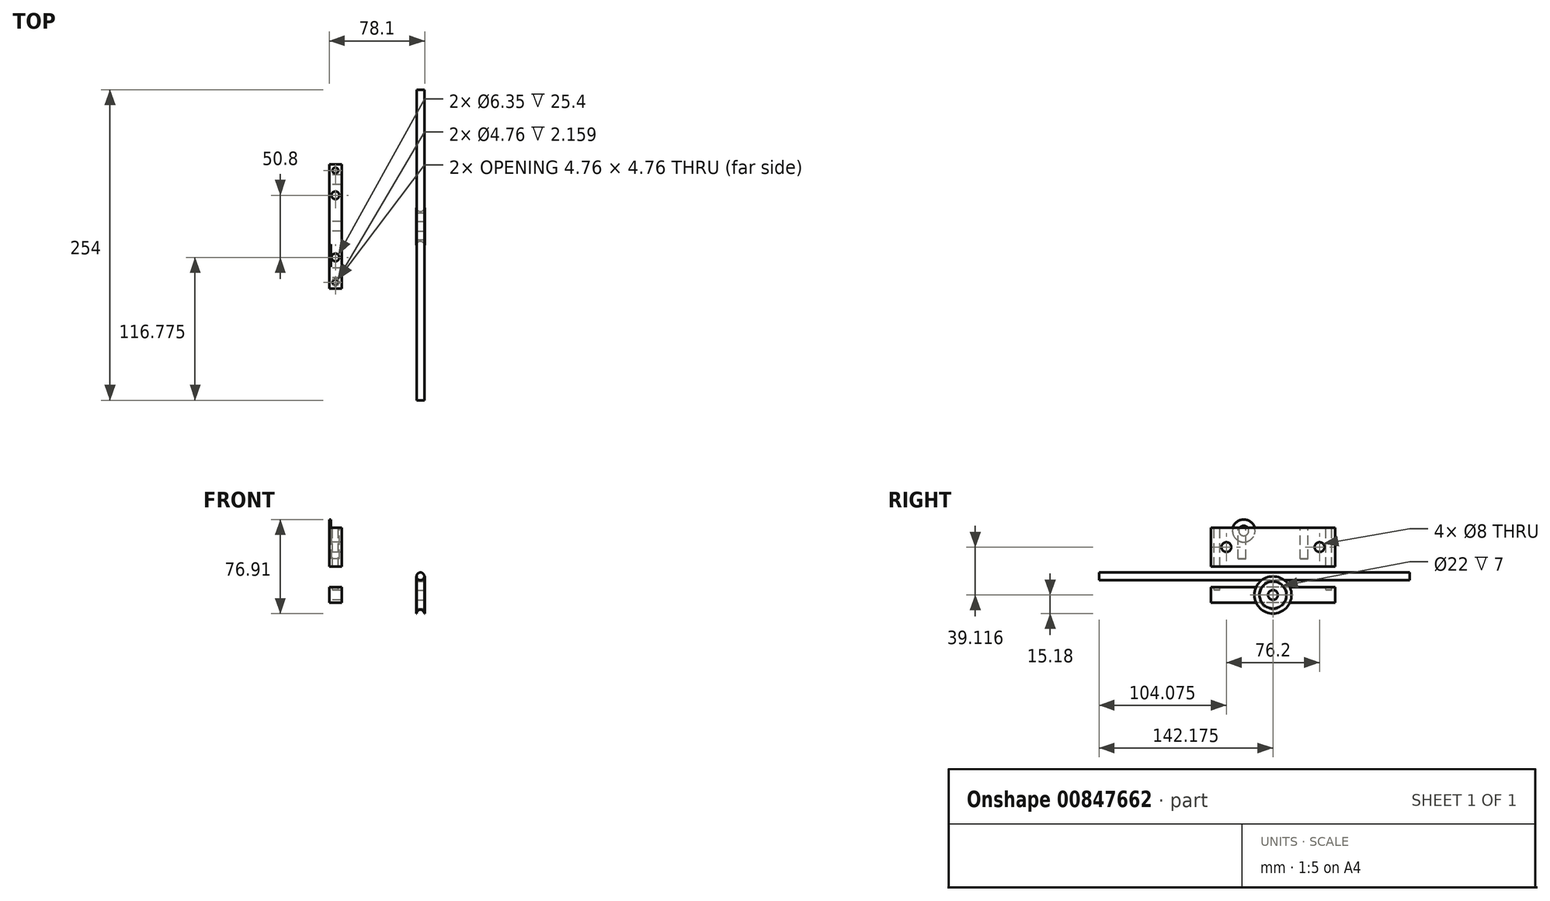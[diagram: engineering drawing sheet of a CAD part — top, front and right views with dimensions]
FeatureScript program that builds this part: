
annotation { "Feature Type Name" : "Feature", "Feature Type Description" : "" }
export const myFeature = defineFeature(function(context is Context, id is Id, definition is map)
    precondition{}
    {
        {
            var Q0;
            Q0=qCreatedBy(makeId("Top.planeOp"),FACE);
            var sketch = newSketch(context, id + "F0", { "sketchPlane" : qUnion([Q0])});
            skArc(sketch, "E0", {"start": v(77.77, 0) * mm, "mid": v(74.6, 3.18) * mm, "end": v(71.42, 0) * mm});
            skLineSegment(sketch, "E1", {"start": v(71.42, 0) * mm, "end": v(71.1, 0) * mm});
            skLineSegment(sketch, "E2", {"start": v(71.1, 0) * mm, "end": v(71.1, 3.18) * mm});
            skLineSegment(sketch, "E3", {"start": v(78.1, 3.18) * mm, "end": v(78.1, 0) * mm});
            skLineSegment(sketch, "E4", {"start": v(77.77, 0) * mm, "end": v(78.1, 0) * mm});
            skPoint(sketch, "E5.0", {"position": v(71.1, 15.18) * mm});
            skLineSegment(sketch, "E6", {"start": v(78.1, 15.18) * mm, "end": v(71.1, 15.18) * mm});
            skLineSegment(sketch, "E7", {"start": v(71.1, 4.18) * mm, "end": v(74.6, 4.18) * mm});
            skLineSegment(sketch, "E8", {"start": v(74.6, 4.18) * mm, "end": v(78.1, 4.18) * mm});
            skLineSegment(sketch, "E9", {"start": v(71.1, 15.18) * mm, "end": v(71.1, 4.18) * mm});
            skLineSegment(sketch, "E10", {"start": v(71.1, 4.18) * mm, "end": v(71.1, 3.18) * mm});
            skLineSegment(sketch, "E11", {"start": v(78.1, 15.18) * mm, "end": v(78.1, 4.18) * mm});
            skLineSegment(sketch, "E12", {"start": v(78.1, 4.18) * mm, "end": v(78.1, 3.18) * mm});
            skSolve(sketch);
        }
        {
            var Q0;
            Q0=qSketchRegion(id+"F0",true);
            var Q1;
            Q1=sQuery(id+"F0.wireOp",EDGE,"E6");
            revolve(context, id + "F1", {"surfaceOperationType" : NewSurfaceOperationType.NEW, "entities" : qUnion([Q0]), "axis" : qUnion([Q1]), "revolveType" : RevolveType.FULL, "oppositeDirection" : true});
        }
        {
            var Q0;
            Q0=makeQuery(id+"F0.imprint","IMPRINT",FACE,{"disambiguationData":[TD([[makeQuery(id+"F0.imprint","IMPRINT",EDGE,{"derivedFrom":sQuery(id+"F0.wireOp",EDGE,"E6")}),1.0]])]});
            var Q1;
            Q1=sQuery(id+"F0.wireOp",EDGE,"E6");
            revolve(context, id + "F2", {"operationType" : NewBodyOperationType.REMOVE, "surfaceOperationType" : NewSurfaceOperationType.NEW, "entities" : qUnion([Q0]), "axis" : qUnion([Q1]), "revolveType" : RevolveType.FULL, "oppositeDirection" : true});
        }
        {
            var Q0;
            Q0=makeQuery(id+"F1.opRevolve","SWEPT_FACE",FACE,{"disambiguationData":[OSD([sQuery(id+"F0.wireOp",EDGE,"E3"),sQuery(id+"F0.wireOp",EDGE,"E11"),sQuery(id+"F0.wireOp",EDGE,"E12")])]});
            var sketch = newSketch(context, id + "F3", { "sketchPlane" : qUnion([Q0])});
            skCircle(sketch, "E13", {"center": v(15.18, 0) * mm, "radius": 11 * mm});
            skCircle(sketch, "E14", {"center": v(15.18, 0) * mm, "radius": 4 * mm});
            skSolve(sketch);
        }
        {
            var Q0;
            Q0=qSketchRegion(id+"F3",true);
            var Q1;
            Q1=sQuery(id+"F3.wireOp",EDGE,"kzQAHwlb-sFjF-DyDI-pdxH-pXrXTPdEGOow");
            var Q2;
            Q2=sQuery(id+"F3.wireOp",EDGE,"E13");
            extrude(context, id + "F4", {"entities" : qUnion([Q0]), "surfaceEntities" : qUnion([Q1, Q2]), "oppositeDirection" : true, "depth" : 7 * mm, "offsetDistance" : 25.4 * mm});
        }
        {
            var Q0;
            Q0=qCreatedBy(makeId("Front.planeOp"),FACE);
            var sketch = newSketch(context, id + "F5", { "sketchPlane" : qUnion([Q0])});
            skCircle(sketch, "E15", {"center": v(74.6, 15.18) * mm, "radius": 3.18 * mm});
            skSolve(sketch);
        }
        {
            var Q0;
            Q0=qSketchRegion(id+"F5",true);
            extrude(context, id + "F6", {"entities" : qUnion([Q0]), "endBound" : BoundingType.SYMMETRIC, "oppositeDirection" : true, "depth" : 254 * mm, "offsetDistance" : 25.4 * mm});
        }
        {
            var Q0;
            Q0=qCreatedBy(makeId("Right.planeOp"),FACE);
            var sketch = newSketch(context, id + "F7", { "sketchPlane" : qUnion([Q0])});
            skCircle(sketch, "E16", {"center": v(-22.92, 39.12) * mm, "radius": 4 * mm});
            skCircle(sketch, "E17.0", {"center": v(53.28, 39.12) * mm, "radius": 4 * mm});
            skCircle(sketch, "E18.0", {"center": v(15.18, 0) * mm, "radius": 4 * mm});
            skLineSegment(sketch, "E19.bottom", {"start": v(65.98, -6.35) * mm, "end": v(-35.62, -6.35) * mm});
            skLineSegment(sketch, "E19.top", {"start": v(65.98, 6.35) * mm, "end": v(-35.62, 6.35) * mm});
            skLineSegment(sketch, "E19.left", {"start": v(65.98, -6.35) * mm, "end": v(65.98, 6.35) * mm});
            skLineSegment(sketch, "E19.right", {"start": v(-35.62, -6.35) * mm, "end": v(-35.62, 6.35) * mm});
            skLineSegment(sketch, "E20.bottom", {"start": v(65.98, 23.24) * mm, "end": v(-35.62, 23.24) * mm});
            skLineSegment(sketch, "E20.top", {"start": v(65.98, 55) * mm, "end": v(-35.62, 55) * mm});
            skLineSegment(sketch, "E20.left", {"start": v(65.98, 23.24) * mm, "end": v(65.98, 55) * mm});
            skLineSegment(sketch, "E20.right", {"start": v(-35.62, 23.24) * mm, "end": v(-35.62, 55) * mm});
            skPoint(sketch, "E20.middle", {"position": v(15.18, 39.12) * mm});
            skLineSegment(sketch, "E21", {"start": v(-35.62, 39.12) * mm, "end": v(65.98, 39.12) * mm, "construction": true});
            skSolve(sketch);
        }
        {
            var Q0;
            Q0 = qSketchRegion(id + "F7", true);
            extrude(context, id + "F8", {"entities" : qUnion([Q0]), "depth" : 10.16 * mm, "offsetDistance" : 25.4 * mm});
        }
        {
            var Q0;
            Q0=makeQuery(id+"F8.opExtrude","SWEPT_FACE",FACE,{"disambiguationData":[OSD([sQuery(id+"F7.wireOp",EDGE,"E20.top")])]});
            var sketch = newSketch(context, id + "F9", { "sketchPlane" : qUnion([Q0])});
            skPoint(sketch, "E22.0", {"position": v(5.08, -35.62) * mm});
            skLineSegment(sketch, "E23", {"start": v(5.08, -35.62) * mm, "end": v(5.08, 15.18) * mm, "construction": true});
            skCircle(sketch, "E24", {"center": v(5.08, 60.9) * mm, "radius": 2.38 * mm});
            skCircle(sketch, "E25", {"center": v(5.08, -30.54) * mm, "radius": 2.38 * mm});
            skLineSegment(sketch, "E26", {"start": v(5.08, 15.18) * mm, "end": v(5.08, 65.98) * mm, "construction": true});
            skCircle(sketch, "E27", {"center": v(5.08, 40.58) * mm, "radius": 3.18 * mm});
            skCircle(sketch, "E28", {"center": v(5.08, -10.22) * mm, "radius": 3.18 * mm});
            skSolve(sketch);
        }
        {
            var Q0;
            Q0=makeQuery(id+"F8.opExtrude","SWEPT_FACE",FACE,{"disambiguationData":[OSD([sQuery(id+"F7.wireOp",EDGE,"E20.top")])]});
            var sketch = newSketch(context, id + "F10", { "sketchPlane" : qUnion([Q0])});
            skCircle(sketch, "E29.0", {"center": v(63.24, 53.28) * mm, "radius": 2.38 * mm});
            skCircle(sketch, "E29.1", {"center": v(83.18, 53.28) * mm, "radius": 2.38 * mm});
            skCircle(sketch, "E29.2", {"center": v(83.18, -22.92) * mm, "radius": 2.38 * mm});
            skCircle(sketch, "E29.3", {"center": v(63.24, -22.92) * mm, "radius": 2.38 * mm});
            skSolve(sketch);
        }
        {
            var Q0;
            Q0=qCreatedBy(makeId("Right.planeOp"),FACE);
            var sketch = newSketch(context, id + "F11", { "sketchPlane" : qUnion([Q0])});
            skCircle(sketch, "E30", {"center": v(-8.7, 52.48) * mm, "radius": 9.25 * mm});
            skCircle(sketch, "E31", {"center": v(-8.7, 52.48) * mm, "radius": 4.09 * mm});
            skSolve(sketch);
        }
        {
            var Q0;
            Q0 = qSketchRegion(id + "F11", true);
            extrude(context, id + "F12", {"entities" : qUnion([Q0]), "depth" : 1.35 * mm, "offsetDistance" : 25.4 * mm});
        }
        {
            var Q0;
            Q0=makeQuery(id+"F9.imprint","IMPRINT",FACE,{"disambiguationData":[TD([[makeQuery(id+"F9.imprint","IMPRINT",EDGE,{"derivedFrom":sQuery(id+"F9.wireOp",EDGE,"E24")}),1.0]])]});
            var Q1;
            Q1=makeQuery(id+"F9.imprint","IMPRINT",FACE,{"disambiguationData":[TD([[makeQuery(id+"F9.imprint","IMPRINT",EDGE,{"derivedFrom":sQuery(id+"F9.wireOp",EDGE,"E25")}),1.0]])]});
            var Q2;
            Q2=sQuery(id+"F9.wireOp",EDGE,"E24");
            var Q3;
            Q3=sQuery(id+"F9.wireOp",EDGE,"E25");
            extrude(context, id + "F13", {"entities" : qUnion([Q0, Q1]), "operationType" : NewBodyOperationType.REMOVE, "surfaceEntities" : qUnion([Q2, Q3]), "oppositeDirection" : true, "depth" : 50.8 * mm, "offsetDistance" : 25.4 * mm});
        }
        {
            var Q0;
            Q0=makeQuery(id+"F9.imprint","IMPRINT",FACE,{"disambiguationData":[TD([[makeQuery(id+"F9.imprint","IMPRINT",EDGE,{"derivedFrom":sQuery(id+"F9.wireOp",EDGE,"E27")}),1.0]])]});
            var Q1;
            Q1=makeQuery(id+"F9.imprint","IMPRINT",FACE,{"disambiguationData":[TD([[makeQuery(id+"F9.imprint","IMPRINT",EDGE,{"derivedFrom":sQuery(id+"F9.wireOp",EDGE,"E28")}),1.0]])]});
            var Q2;
            Q2=sQuery(id+"F9.wireOp",EDGE,"E27");
            var Q3;
            Q3=sQuery(id+"F9.wireOp",EDGE,"E28");
            extrude(context, id + "F14", {"entities" : qUnion([Q0, Q1]), "operationType" : NewBodyOperationType.REMOVE, "surfaceEntities" : qUnion([Q2, Q3]), "oppositeDirection" : true, "depth" : 25.4 * mm, "offsetDistance" : 25.4 * mm});
        }
    });
